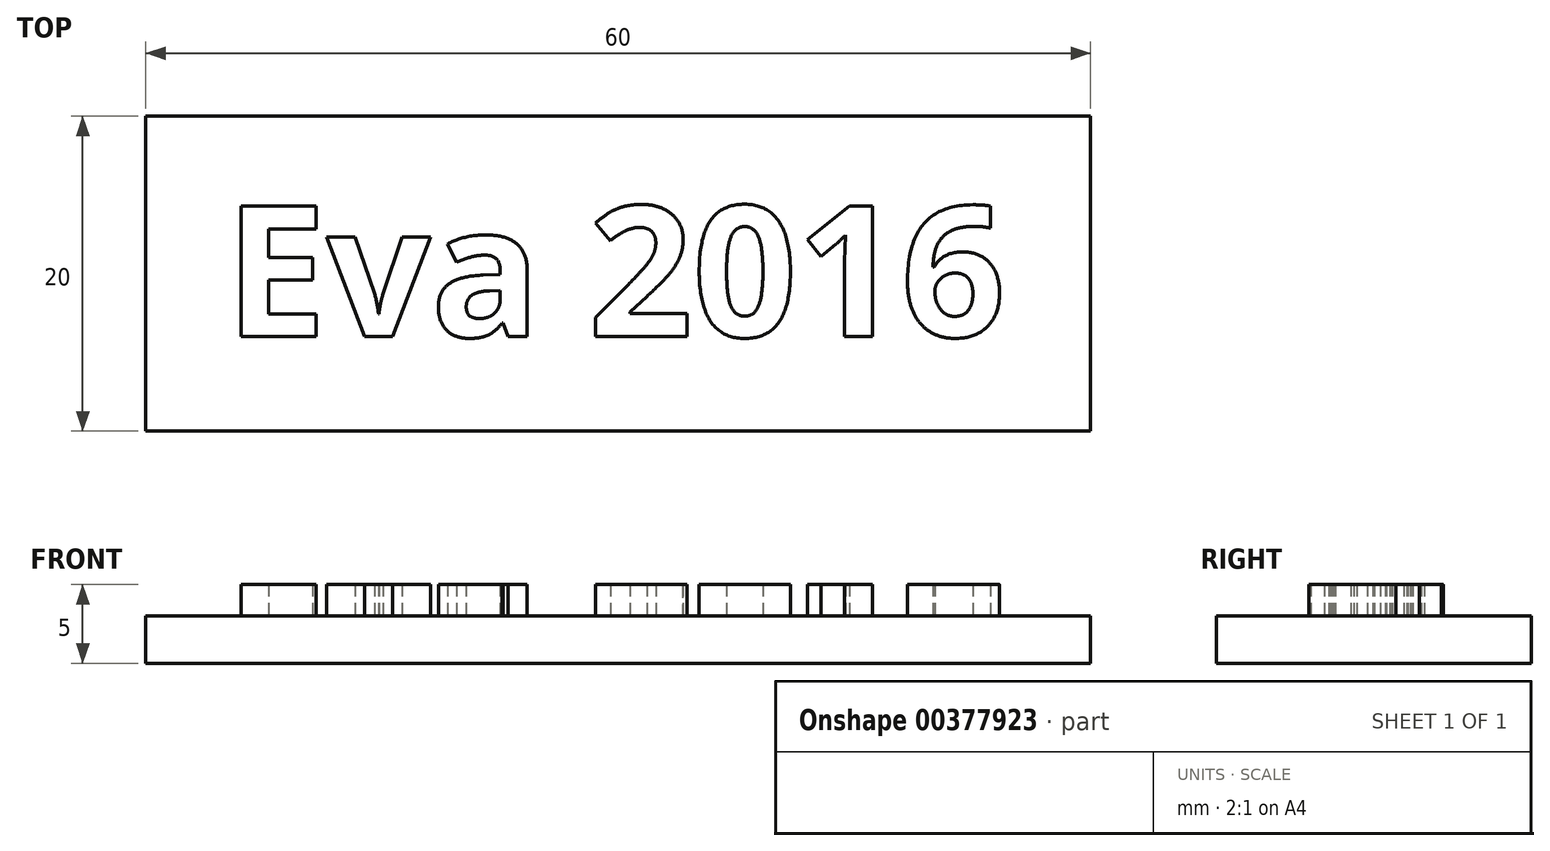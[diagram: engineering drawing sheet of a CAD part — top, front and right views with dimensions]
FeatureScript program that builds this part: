
annotation { "Feature Type Name" : "Feature", "Feature Type Description" : "" }
export const myFeature = defineFeature(function(context is Context, id is Id, definition is map)
    precondition{}
    {
        {
            var Q0;
            Q0=qCreatedBy(makeId("Top.planeOp"),FACE);
            var sketch = newSketch(context, id + "F0", { "sketchPlane" : qUnion([Q0])});
            skLineSegment(sketch, "E0.bottom", {"start": v(-33.75, -29.18) * mm, "end": v(26.25, -29.18) * mm});
            skLineSegment(sketch, "E0.top", {"start": v(-33.75, -9.18) * mm, "end": v(26.25, -9.18) * mm});
            skLineSegment(sketch, "E0.left", {"start": v(-33.75, -29.18) * mm, "end": v(-33.75, -9.18) * mm});
            skLineSegment(sketch, "E0.right", {"start": v(26.25, -29.18) * mm, "end": v(26.25, -9.18) * mm});
            skSolve(sketch);
        }
        {
            var Q0;
            Q0=makeQuery(id+"F0.imprint","IMPRINT",FACE,{"disambiguationData":[TD([[makeQuery(id+"F0.imprint","IMPRINT",EDGE,{"derivedFrom":sQuery(id+"F0.wireOp",EDGE,"E0.bottom")}),1.0]])]});
            extrude(context, id + "F1", {"entities" : qUnion([Q0]), "depth" : 3 * mm});
        }
        {
            var Q0;
            Q0=makeQuery(id+"F1.opExtrude","CAP_FACE",FACE,{"disambiguationData":[OSD([sQuery(id+"F0.wireOp",EDGE,"E0.bottom"),sQuery(id+"F0.wireOp",EDGE,"E0.top"),sQuery(id+"F0.wireOp",EDGE,"E0.left"),sQuery(id+"F0.wireOp",EDGE,"E0.right")])],"isStart":false});
            var sketch = newSketch(context, id + "F2", { "sketchPlane" : qUnion([Q0])});
            skText(sketch, "E1", { "text": "Eva 2016", "fontName": "OpenSans-Bold.ttf"});
            const initialGuessF2  = {"E1": [-0.02875, -0.02318, 1, 0, 0.00835]};
            skSetInitialGuess(sketch, initialGuessF2);
            skSolve(sketch);
        }
        {
            var Q0;
            Q0=makeQuery(id+"F2.imprint","IMPRINT",FACE,{"disambiguationData":[TD([[makeQuery(id+"F2.imprint","IMPRINT",EDGE,{"derivedFrom":sQuery(id+"F2.wireOp",EDGE,"E1.sketch_text.stroke-71")}),-1.0]])]});
            var Q1;
            Q1=makeQuery(id+"F2.imprint","IMPRINT",FACE,{"disambiguationData":[TD([[makeQuery(id+"F2.imprint","IMPRINT",EDGE,{"derivedFrom":sQuery(id+"F2.wireOp",EDGE,"E1.sketch_text.stroke-87")}),-1.0]])]});
            var Q2;
            Q2=makeQuery(id+"F2.imprint","IMPRINT",FACE,{"disambiguationData":[TD([[makeQuery(id+"F2.imprint","IMPRINT",EDGE,{"derivedFrom":sQuery(id+"F2.wireOp",EDGE,"E1.sketch_text.stroke-97")}),-1.0]])]});
            var Q3;
            Q3=makeQuery(id+"F2.imprint","IMPRINT",FACE,{"disambiguationData":[TD([[makeQuery(id+"F2.imprint","IMPRINT",EDGE,{"derivedFrom":sQuery(id+"F2.wireOp",EDGE,"E1.sketch_text.stroke-47")}),-1.0]])]});
            var Q4;
            Q4=makeQuery(id+"F2.imprint","IMPRINT",FACE,{"disambiguationData":[TD([[makeQuery(id+"F2.imprint","IMPRINT",EDGE,{"derivedFrom":sQuery(id+"F2.wireOp",EDGE,"E1.sketch_text.stroke-22")}),-1.0]])]});
            var Q5;
            Q5=makeQuery(id+"F2.imprint","IMPRINT",FACE,{"disambiguationData":[TD([[makeQuery(id+"F2.imprint","IMPRINT",EDGE,{"derivedFrom":sQuery(id+"F2.wireOp",EDGE,"E1.sketch_text.stroke-12")}),-1.0]])]});
            var Q6;
            Q6=makeQuery(id+"F2.imprint","IMPRINT",FACE,{"disambiguationData":[TD([[makeQuery(id+"F2.imprint","IMPRINT",EDGE,{"derivedFrom":sQuery(id+"F2.wireOp",EDGE,"E1.sketch_text.stroke-0")}),-1.0]])]});
            extrude(context, id + "F3", {"entities" : qUnion([Q0, Q1, Q2, Q3, Q4, Q5, Q6]), "operationType" : NewBodyOperationType.ADD, "depth" : 2 * mm});
        }
    });
